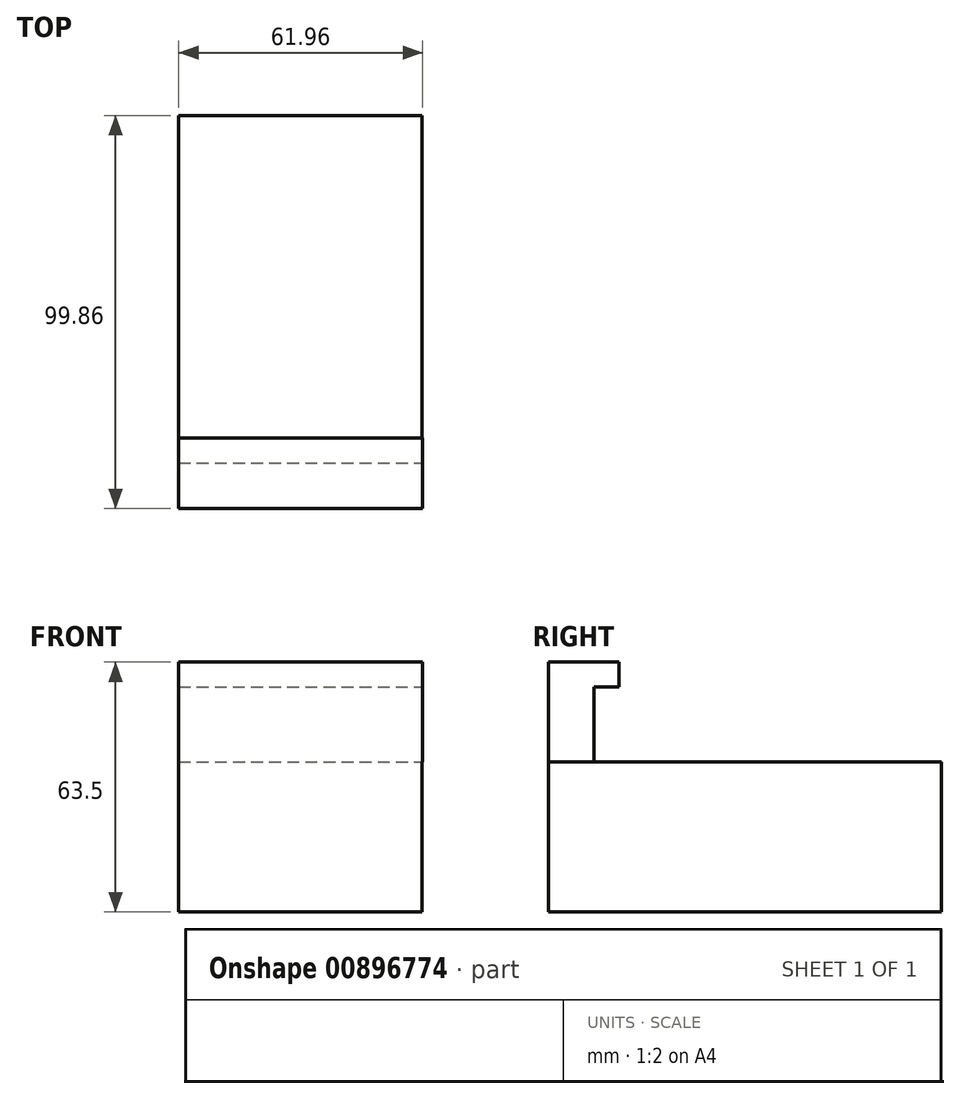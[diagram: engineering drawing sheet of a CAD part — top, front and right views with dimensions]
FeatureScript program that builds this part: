
annotation { "Feature Type Name" : "Feature", "Feature Type Description" : "" }
export const myFeature = defineFeature(function(context is Context, id is Id, definition is map)
    precondition{}
    {
        {
            var Q0;
            Q0=qCreatedBy(makeId("Top.planeOp"),FACE);
            var sketch = newSketch(context, id + "F0", { "sketchPlane" : qUnion([Q0])});
            skLineSegment(sketch, "E0.bottom", {"start": v(-30.94, 49.93) * mm, "end": v(30.94, 49.93) * mm});
            skLineSegment(sketch, "E0.top", {"start": v(-30.94, -49.93) * mm, "end": v(30.94, -49.93) * mm});
            skLineSegment(sketch, "E0.left", {"start": v(-30.94, 49.93) * mm, "end": v(-30.94, -49.93) * mm});
            skLineSegment(sketch, "E0.right", {"start": v(30.94, 49.93) * mm, "end": v(30.94, -49.93) * mm});
            skPoint(sketch, "E0.middle", {"position": v(0, 0) * mm});
            skSolve(sketch);
        }
        {
            var Q0;
            Q0=qCreatedBy(makeId("Top.planeOp"),FACE);
            var sketch = newSketch(context, id + "F1", { "sketchPlane" : qUnion([Q0])});
            skLineSegment(sketch, "E1.bottom", {"start": v(-30.95, -49.93) * mm, "end": v(31.01, -49.93) * mm});
            skLineSegment(sketch, "E1.top", {"start": v(-30.95, -38.37) * mm, "end": v(31.01, -38.37) * mm});
            skLineSegment(sketch, "E1.left", {"start": v(-30.95, -49.93) * mm, "end": v(-30.95, -38.37) * mm});
            skLineSegment(sketch, "E1.right", {"start": v(31.01, -49.93) * mm, "end": v(31.01, -38.37) * mm});
            skSolve(sketch);
        }
        {
            var Q0;
            Q0 = qSketchRegion(id + "F1", true);
            extrude(context, id + "F2", {"entities" : qUnion([Q0]), "depth" : 25.4 * mm, "offsetDistance" : 25.4 * mm});
        }
        {
            var Q0;
            Q0 = qSketchRegion(id + "F0", true);
            extrude(context, id + "F3", {"entities" : qUnion([Q0]), "operationType" : NewBodyOperationType.ADD, "oppositeDirection" : true, "depth" : 38.1 * mm, "offsetDistance" : 25.4 * mm});
        }
        {
            var Q0;
            Q0=makeQuery(id+"F2.opExtrude","SWEPT_FACE",FACE,{"disambiguationData":[OSD([sQuery(id+"F1.wireOp",EDGE,"E1.top")])]});
            var sketch = newSketch(context, id + "F4", { "sketchPlane" : qUnion([Q0])});
            skLineSegment(sketch, "E2.bottom", {"start": v(30.95, 19.05) * mm, "end": v(-31.01, 19.05) * mm});
            skLineSegment(sketch, "E2.top", {"start": v(30.95, 25.4) * mm, "end": v(-31.01, 25.4) * mm});
            skLineSegment(sketch, "E2.left", {"start": v(30.95, 19.05) * mm, "end": v(30.95, 25.4) * mm});
            skLineSegment(sketch, "E2.right", {"start": v(-31.01, 19.05) * mm, "end": v(-31.01, 25.4) * mm});
            skSolve(sketch);
        }
        {
            var Q0;
            Q0 = qSketchRegion(id + "F4", true);
            extrude(context, id + "F5", {"entities" : qUnion([Q0]), "operationType" : NewBodyOperationType.ADD, "depth" : 6.35 * mm, "offsetDistance" : 25.4 * mm});
        }
    });
